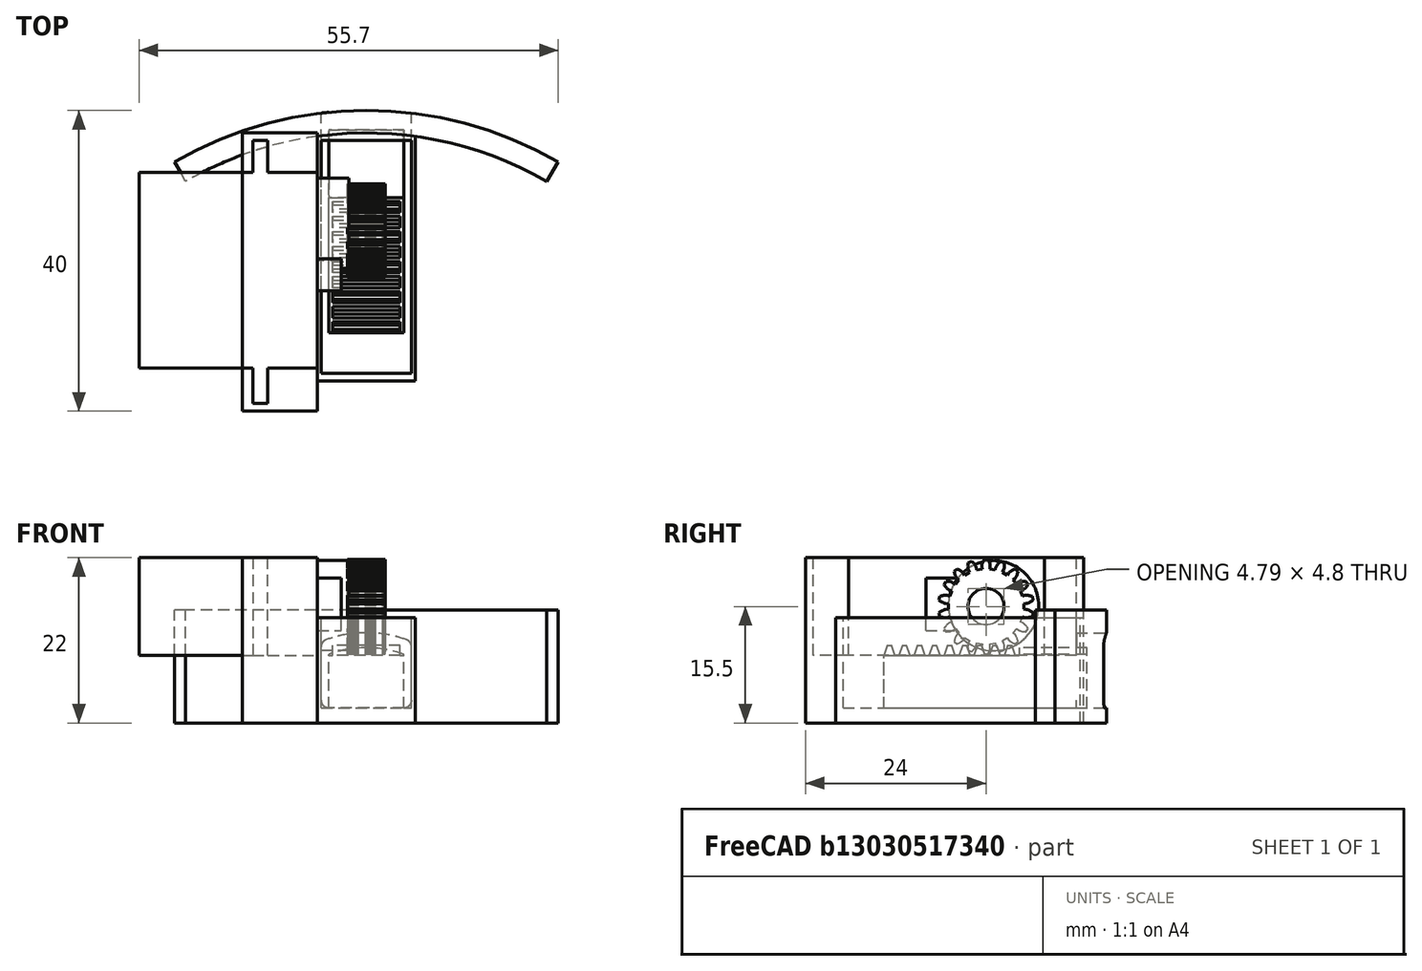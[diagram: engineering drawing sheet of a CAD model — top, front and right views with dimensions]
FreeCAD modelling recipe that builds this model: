
FCSTD DOCUMENT  (FreeCAD 0.16R4924 (Git))
Label: interior_servo_bay_v4p12
License: All rights reserved
LicenseURL: http://en.wikipedia.org/wiki/All_rights_reserved
objects: Part::Feature×11, Part::Box×9, Part::Cut×5, Part::MultiFuse×5, Part::Cylinder×4, Part::Extrusion×3, Part::Thickness×1, Mesh::Feature×1, Part::Fuse×1, Part::FeaturePython×1, Part::Prism×1, Part::MultiCommon×1
note: 42 computed .brp shape members not serialized (recipe doc carries the construction recipe); baked Part::Feature solids carry a one-line shape summary decoded from their .brp

FEATURE [Part::Cylinder] Cylinder  label="bottle_wall"
  Angle = 60
  Height = 15
  Placement = pos=(8.5,-7,0) rot=(0,0,1;1.0472rad)
  Radius = 51
FEATURE [Part::Cylinder] Cylinder001  label="bottle_wall001"
  Angle = 60
  Height = 15
  Placement = pos=(8.5,-7,0) rot=(0,0,1;1.0472rad)
  Radius = 48
FEATURE [Part::Cut] Cut  label="bottle_wall_composite"
  Base = -> Cylinder
  Placement = pos=(0,-2,0) rot=(0,0,1;0rad)
  Tool = -> Cylinder001
FEATURE [Part::Feature] Common_cs  label="pin_cs"
  Placement = pos=(3.5,35,2) rot=(0,0,1;0rad)
  shape: bbox 10 x 2e-07 x 8 mm, 0 faces, 0 solids (baked)
FEATURE [Part::Extrusion] Extrude
  Base = -> Common_cs
  Dir = (0,5,0)
  Solid = true
FEATURE [Part::Thickness] Thickness
  Faces = -> Extrude [Face7]
  Intersection = false
  Join = 0
  Mode = 0
  SelfIntersection = false
  Value = 1
FEATURE [Part::Feature] Common_cs001  label="pin_cs001"
  Placement = pos=(3.5,35,2) rot=(0,0,1;0rad)
  shape: bbox 10 x 2e-07 x 8 mm, 0 faces, 0 solids (baked)
FEATURE [Part::Extrusion] Extrude001
  Base = -> Common_cs001
  Dir = (0,5,0)
  Solid = true
FEATURE [Part::MultiFuse] Fusion  label="bolt_bottle_side_opening"
  Placement = pos=(0,-7,1) rot=(0,0,1;0rad)
  Shapes = -> [Thickness,Extrude,Extrude001]
FEATURE [Part::Box] Box  label="pullBay"
  Height = 15
  Length = 12
  Placement = pos=(2.5,7,2) rot=(0,0,1;0rad)
  Width = 31
FEATURE [Part::Box] Box001  label="Case"
  Height = 14
  Length = 13
  Placement = pos=(2,6,0) rot=(0,0,1;0rad)
  Width = 34
FEATURE [Part::Cut] Cut001  label="cut bay from case"
  Base = -> Box001
  Tool = -> Box
FEATURE [Part::MultiFuse] Fusion001  label="wall plus case"
  Shapes = -> [Cut,Cut001]
FEATURE [Part::Cut] Cut002  label="hole cut out of case"
  Base = -> Fusion001
  Tool = -> Fusion
FEATURE [Mesh::Feature] Mesh  label="servo_motor_2"
  Placement = pos=(33.6,-52,22) rot=(0,0,-1;1.5708rad)
FEATURE [Part::Fuse] union  label="pinion"
FEATURE [Part::FeaturePython] RefineLinearExtrude  # WARN: FeaturePython — macro-defined, semantics opaque (R4)
  Base = -> union
FEATURE [Part::Extrusion] LinearExtrude
  Base = -> RefineLinearExtrude
  Dir = (0,0,5)
  Solid = true
FEATURE [Part::Prism] prism
  Circumradius = 2.4
  Height = 7
  Placement = pos=(0,0,-1) rot=(0,0,1;0rad)
  Polygon = 50
FEATURE [Part::Cut] difference  label="pinion_final"
  Base = -> LinearExtrude
  Placement = pos=(6,26,15.5) rot=(0,1,0;1.5708rad)
  Tool = -> prism
FEATURE [Part::Cylinder] Cylinder002  label="rounded_top"
  Angle = 360
  Height = 40
  Placement = pos=(5,35,-7) rot=(1,0,0;1.5708rad)
  Radius = 15
FEATURE [Part::Box] Box005  label="pin"
  Height = 8
  Length = 10
  Width = 27
FEATURE [Part::MultiCommon] Common  label="rounded pin"
  Shapes = -> [Cylinder002,Box005]
FEATURE [Part::Box] Box006  label="flat_top"
  Height = 10
  Length = 10
  Placement = pos=(0,0,7) rot=(0,0,1;0rad)
  Width = 18
FEATURE [Part::Cut] Cut005
  Base = -> Common
  Placement = pos=(0,11,0) rot=(0,0,1;0rad)
  Tool = -> Box006
FEATURE [Part::Box] cube
  Height = 5
  Length = 18
  Placement = pos=(-12,-4.5,-2.5) rot=(0,0,1;0rad)
  Width = 9
FEATURE [Part::Feature] polyhedron
  Placement = pos=(-11.2451,0,2.5) rot=(0,0,1;0rad)
  shape: bbox 1.51 x 9 x 1.337 mm, 6 faces (baked)
FEATURE [Part::Feature] polyhedron001
  Placement = pos=(-9.24512,0,2.5) rot=(0,0,1;0rad)
  shape: bbox 1.51 x 9 x 1.337 mm, 6 faces (baked)
FEATURE [Part::Feature] polyhedron002
  Placement = pos=(-7.24512,0,2.5) rot=(0,0,1;0rad)
  shape: bbox 1.51 x 9 x 1.337 mm, 6 faces (baked)
FEATURE [Part::Feature] polyhedron003
  Placement = pos=(-5.24512,0,2.5) rot=(0,0,1;0rad)
  shape: bbox 1.51 x 9 x 1.337 mm, 6 faces (baked)
FEATURE [Part::Feature] polyhedron004
  Placement = pos=(-3.24512,0,2.5) rot=(0,0,1;0rad)
  shape: bbox 1.51 x 9 x 1.337 mm, 6 faces (baked)
FEATURE [Part::Feature] polyhedron005
  Placement = pos=(-1.24512,0,2.5) rot=(0,0,1;0rad)
  shape: bbox 1.51 x 9 x 1.337 mm, 6 faces (baked)
FEATURE [Part::Feature] polyhedron006
  Placement = pos=(0.754882,0,2.5) rot=(0,0,1;0rad)
  shape: bbox 1.51 x 9 x 1.337 mm, 6 faces (baked)
FEATURE [Part::Feature] polyhedron007
  Placement = pos=(2.75488,0,2.5) rot=(0,0,1;0rad)
  shape: bbox 1.51 x 9 x 1.337 mm, 6 faces (baked)
FEATURE [Part::Feature] polyhedron008
  Placement = pos=(4.75488,0,2.5) rot=(0,0,1;0rad)
  shape: bbox 1.51 x 9 x 1.337 mm, 6 faces (baked)
FEATURE [Part::MultiFuse] Fusion003  label="rack"
  Placement = pos=(5,23,4.5) rot=(0,0,1;1.5708rad)
  Shapes = -> [cube,polyhedron002,polyhedron003,polyhedron004,polyhedron005,polyhedron,polyhedron007,polyhedron001,polyhedron006,polyhedron008]
FEATURE [Part::MultiFuse] Fusion004  label="pin_3p2"
  Placement = pos=(3.5,1.4,2) rot=(0,0,1;0rad)
  Shapes = -> [Fusion003,Cut005]
FEATURE [Part::Box] Box007  label="mount"
  Height = 22
  Length = 10
  Placement = pos=(-8,2,0) rot=(0,0,1;0rad)
  Width = 37
FEATURE [Part::Box] Box008  label="Cube"
  Height = 13
  Length = 35
  Placement = pos=(-42,1.5,-2) rot=(0,0,1;0rad)
  Width = 2
FEATURE [Part::Box] Box009  label="Cube001"
  Height = 13
  Length = 26
  Placement = pos=(-37.75,-13.6,-2) rot=(0,0,1;0rad)
  Width = 23.7
FEATURE [Part::Box] Box010  label="Cube002"
  Height = 7
  Length = 10
  Placement = pos=(-32,3.3,1.3) rot=(0,0,1;0rad)
  Width = 10
FEATURE [Part::Cylinder] Cylinder003
  Angle = 360
  Height = 6
  Placement = pos=(-31,14.3,4.6) rot=(1,0,0;1.5708rad)
  Radius = 6
FEATURE [Part::MultiFuse] Fusion005  label="simple_servo_rev_eng"
  Placement = pos=(-8.1,-4,11) rot=(0,0,1;4.71239rad)
  Shapes = -> [Box008,Box010,Cylinder003,Box009]
